# Revit family: STO24430BR_STO24430PTO
name_source: partatom
category: Dispositivos elétricos
units: mm (PartAtom-declared; Revit-internal decimal feet)

## family parameters
Compartilhado = Sim
Corte com vazios quando carregada = Sim
Cota do conector redondo = Utilizar diâmetro
Hospedeiro = Parede
Manter orientação da anotação = Não
Número OmniClass = 23.80.70.00
Ponto de cálculo do ambiente = Não
Sempre na vertical = Sim
Tipo de parte = Normal
Título OmniClass = Lighting

## types (2) — shared parameters
Altura = 0.13 m
Comprimento = 0.09 m
Corrente máxima de saída = 10 A
Fabricante = Stella
Largura = 0.01 m
Modelo = Tomada 10A + Tomada dupla USB-C S.TOUCH

Tomada dupla 10A S.TOUCH

Tomada dupla 10A S.TOUCH
Tensão máxima = 250V
URL = https://stella.com.br
zero-valued in all types: Elevação padrão

## per-type parameters (varying)
| type | Estrutura | Referência |
| ST024430BR - BRANCO - TOMADA 10A + USB-C 2,4A | Al Branco | STO24430BR |
| ST024430PTO - PRETO - TOMADA 10A + USB-C 2,4A | Al - Preto | STO24430PTO |
